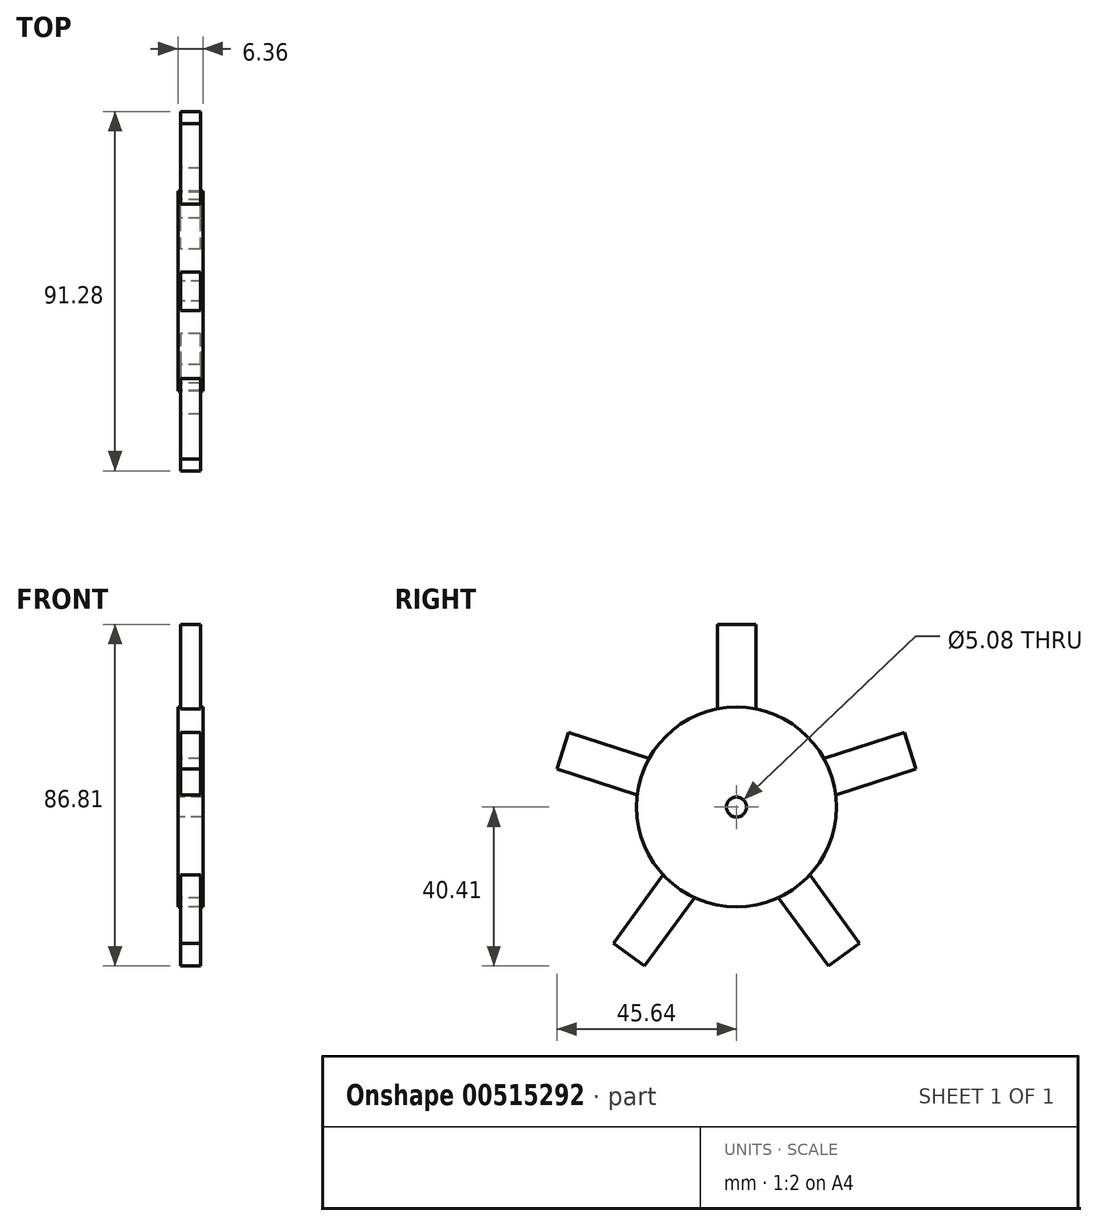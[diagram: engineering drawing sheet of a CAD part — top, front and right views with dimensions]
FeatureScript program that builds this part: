
annotation { "Feature Type Name" : "Feature", "Feature Type Description" : "" }
export const myFeature = defineFeature(function(context is Context, id is Id, definition is map)
    precondition{}
    {
        {
            var Q0;
            Q0=qCreatedBy(makeId("Front.planeOp"),FACE);
            var sketch = newSketch(context, id + "F0", { "sketchPlane" : qUnion([Q0])});
            skCircle(sketch, "E0", {"center": v(0, 63.5) * mm, "radius": 19.05 * mm});
            skLineSegment(sketch, "E1", {"start": v(0, 0) * mm, "end": v(-59.05, 0) * mm, "construction": true});
            skSolve(sketch);
        }
        {
            var Q0;
            Q0=sQuery(id+"F0.wireOp",EDGE,"E1");
            var Q1;
            Q1=sQuery(id+"F0.wireOp",EDGE,"E0");
            var Q2;
            Q2=sQuery(id+"F0.wireOp",EDGE,"E1");
            revolve(context, id + "F1", {"bodyType" : ToolBodyType.SURFACE, "surfaceEntities" : qUnion([Q0, Q1]), "axis" : qUnion([Q2]), "revolveType" : RevolveType.FULL});
        }
        {
            var Q0;
            Q0=qCreatedBy(makeId("Right.planeOp"),FACE);
            var sketch = newSketch(context, id + "F2", { "sketchPlane" : qUnion([Q0])});
            skCircle(sketch, "E2", {"center": v(0, 0) * mm, "radius": 25.4 * mm});
            skCircle(sketch, "E3", {"center": v(0, 0) * mm, "radius": 2.54 * mm});
            skSolve(sketch);
        }
        {
            var Q0;
            Q0 = qSketchRegion(id + "F2", true);
            extrude(context, id + "F3", {"entities" : qUnion([Q0]), "endBound" : BoundingType.SYMMETRIC, "depth" : 6.35 * mm, "offsetDistance" : 25.4 * mm});
        }
        {
            var Q0;
            Q0=qCreatedBy(makeId("Right.planeOp"),FACE);
            var sketch = newSketch(context, id + "F4", { "sketchPlane" : qUnion([Q0])});
            skLineSegment(sketch, "E4.bottom", {"start": v(-4.9, 24.92) * mm, "end": v(4.9, 24.92) * mm});
            skLineSegment(sketch, "E4.top", {"start": v(-4.9, 46.4) * mm, "end": v(4.9, 46.4) * mm});
            skLineSegment(sketch, "E4.left", {"start": v(-4.9, 24.92) * mm, "end": v(-4.9, 46.4) * mm});
            skLineSegment(sketch, "E4.right", {"start": v(4.9, 24.92) * mm, "end": v(4.9, 46.4) * mm});
            skLineSegment(sketch, "E5", {"start": v(0, 46.4) * mm, "end": v(0, 0) * mm, "construction": true});
            skPoint(sketch, "E6", {"position": v(0, 46.4) * mm});
            skLineSegment(sketch, "E7.1.0", {"start": v(-25.22, 3.05) * mm, "end": v(-45.64, 9.69) * mm});
            skLineSegment(sketch, "E7.1.1", {"start": v(-45.64, 9.69) * mm, "end": v(-42.62, 18.99) * mm});
            skLineSegment(sketch, "E7.1.2", {"start": v(-22.2, 12.35) * mm, "end": v(-42.62, 18.99) * mm});
            skLineSegment(sketch, "E7.1.3", {"start": v(-25.22, 3.05) * mm, "end": v(-22.2, 12.35) * mm});
            skLineSegment(sketch, "E7.2.0", {"start": v(-10.7, -23.04) * mm, "end": v(-23.32, -40.41) * mm});
            skLineSegment(sketch, "E7.2.1", {"start": v(-23.32, -40.41) * mm, "end": v(-31.23, -34.66) * mm});
            skLineSegment(sketch, "E7.2.2", {"start": v(-18.6, -17.3) * mm, "end": v(-31.23, -34.66) * mm});
            skLineSegment(sketch, "E7.2.3", {"start": v(-10.7, -23.04) * mm, "end": v(-18.6, -17.3) * mm});
            skLineSegment(sketch, "E7.3.0", {"start": v(18.6, -17.3) * mm, "end": v(31.23, -34.66) * mm});
            skLineSegment(sketch, "E7.3.1", {"start": v(31.23, -34.66) * mm, "end": v(23.32, -40.41) * mm});
            skLineSegment(sketch, "E7.3.2", {"start": v(10.7, -23.04) * mm, "end": v(23.32, -40.41) * mm});
            skLineSegment(sketch, "E7.3.3", {"start": v(18.6, -17.3) * mm, "end": v(10.7, -23.04) * mm});
            skLineSegment(sketch, "E7.4.0", {"start": v(22.2, 12.35) * mm, "end": v(42.62, 18.99) * mm});
            skLineSegment(sketch, "E7.4.1", {"start": v(42.62, 18.99) * mm, "end": v(45.64, 9.69) * mm});
            skLineSegment(sketch, "E7.4.2", {"start": v(25.22, 3.05) * mm, "end": v(45.64, 9.69) * mm});
            skLineSegment(sketch, "E7.4.3", {"start": v(22.2, 12.35) * mm, "end": v(25.22, 3.05) * mm});
            skPoint(sketch, "E7.center", {"position": v(0, 0) * mm});
            skSolve(sketch);
        }
        {
            var Q0;
            Q0 = qSketchRegion(id + "F4", true);
            extrude(context, id + "F5", {"entities" : qUnion([Q0]), "operationType" : NewBodyOperationType.ADD, "endBound" : BoundingType.SYMMETRIC, "depth" : 5.08 * mm, "offsetDistance" : 25.4 * mm});
        }
    });
